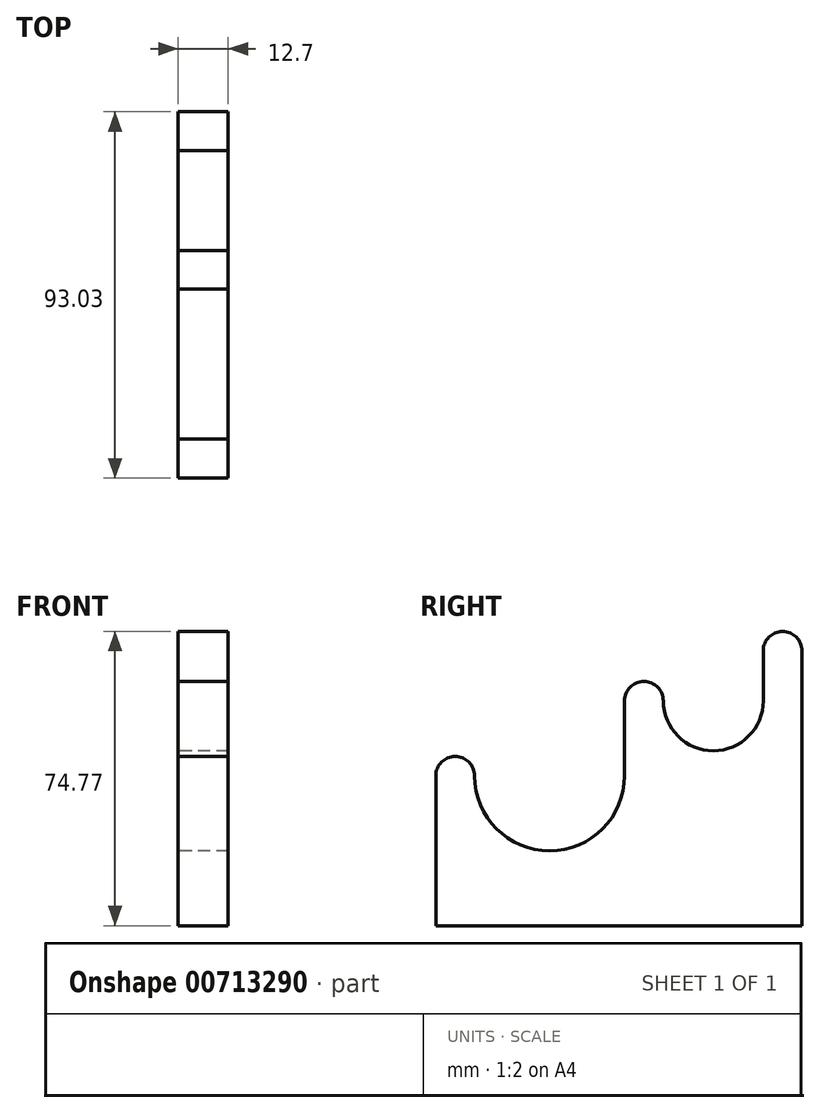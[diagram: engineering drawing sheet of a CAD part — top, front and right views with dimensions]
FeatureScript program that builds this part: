
annotation { "Feature Type Name" : "Feature", "Feature Type Description" : "" }
export const myFeature = defineFeature(function(context is Context, id is Id, definition is map)
    precondition{}
    {
        {
            var Q0;
            Q0=qCreatedBy(makeId("Right.planeOp"),FACE);
            var sketch = newSketch(context, id + "F0", { "sketchPlane" : qUnion([Q0])});
            skLineSegment(sketch, "E0", {"start": v(0, 0) * mm, "end": v(93.03, 0) * mm});
            skLineSegment(sketch, "E1", {"start": v(93.03, 0) * mm, "end": v(93.03, 69.85) * mm});
            skLineSegment(sketch, "E2", {"start": v(0, 0) * mm, "end": v(0, 38.1) * mm});
            skArc(sketch, "E3", {"start": v(9.84, 38.1) * mm, "mid": v(28.9, 19.05) * mm, "end": v(47.94, 38.1) * mm});
            skArc(sketch, "E4", {"start": v(57.79, 57.15) * mm, "mid": v(70.48, 44.45) * mm, "end": v(83.19, 57.15) * mm});
            skArc(sketch, "E5", {"start": v(9.84, 38.1) * mm, "mid": v(4.92, 43.02) * mm, "end": v(0, 38.1) * mm});
            skLineSegment(sketch, "E6", {"start": v(47.94, 38.1) * mm, "end": v(47.94, 57.15) * mm});
            skArc(sketch, "E7", {"start": v(57.79, 57.15) * mm, "mid": v(52.86, 62.07) * mm, "end": v(47.94, 57.15) * mm});
            skLineSegment(sketch, "E8", {"start": v(83.19, 57.15) * mm, "end": v(83.19, 69.85) * mm});
            skArc(sketch, "E9", {"start": v(93.03, 69.85) * mm, "mid": v(88.1, 74.77) * mm, "end": v(83.19, 69.85) * mm});
            skSolve(sketch);
        }
        {
            var Q0;
            Q0 = qSketchRegion(id + "F0", true);
            extrude(context, id + "F1", {"entities" : qUnion([Q0]), "depth" : 12.7 * mm, "offsetDistance" : 25.4 * mm});
        }
    });
